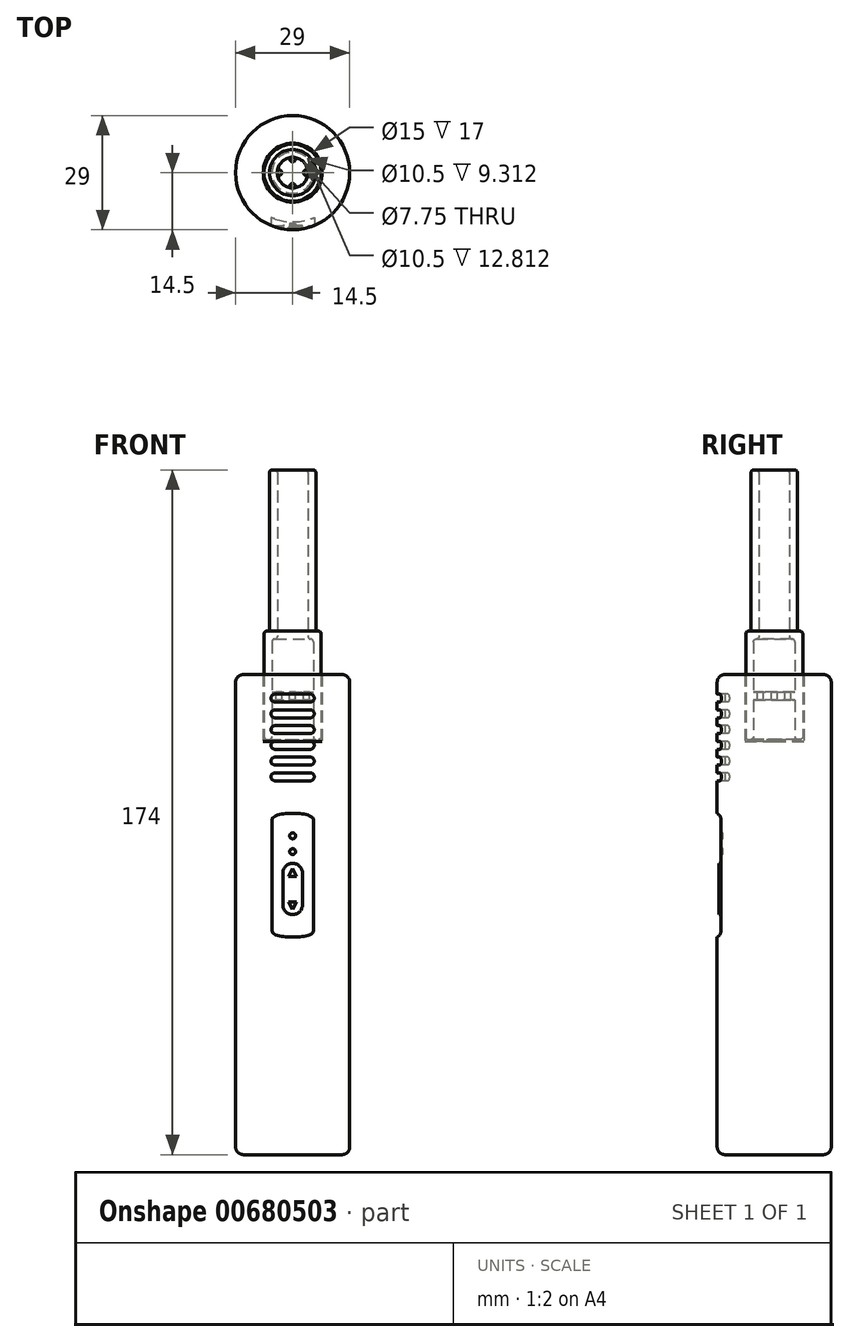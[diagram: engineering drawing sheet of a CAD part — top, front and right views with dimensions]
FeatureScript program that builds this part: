
annotation { "Feature Type Name" : "Feature", "Feature Type Description" : "" }
export const myFeature = defineFeature(function(context is Context, id is Id, definition is map)
    precondition{}
    {
        {
            var Q0;
            Q0=qCreatedBy(makeId("Top.planeOp"),FACE);
            var sketch = newSketch(context, id + "F0", { "sketchPlane" : qUnion([Q0])});
            skCircle(sketch, "E0", {"center": v(0, 0) * mm, "radius": 14.5 * mm});
            skCircle(sketch, "E1", {"center": v(0, 0) * mm, "radius": 7.5 * mm});
            skSolve(sketch);
        }
        {
            var Q0;
            Q0=qCreatedBy(makeId("Front.planeOp"),FACE);
            var sketch = newSketch(context, id + "F1", { "sketchPlane" : qUnion([Q0])});
            skLineSegment(sketch, "E2", {"start": v(0, -17.29) * mm, "end": v(0, 153.89) * mm, "construction": true});
            skSolve(sketch);
        }
        {
            var Q0;
            Q0=makeQuery(id+"F0.imprint","IMPRINT",FACE,{"disambiguationData":[TD([[makeQuery(id+"F0.imprint","IMPRINT",EDGE,{"derivedFrom":sQuery(id+"F0.wireOp",EDGE,"E0")}),1.0]])]});
            extrude(context, id + "F2", {"entities" : qUnion([Q0]), "depth" : 122 * mm, "offsetDistance" : 25 * mm});
        }
        {
            var Q0;
            Q0=makeQuery(id+"F0.imprint","IMPRINT",FACE,{"disambiguationData":[TD([[makeQuery(id+"F0.imprint","IMPRINT",EDGE,{"derivedFrom":sQuery(id+"F0.wireOp",EDGE,"E1")}),1.0]])]});
            extrude(context, id + "F3", {"entities" : qUnion([Q0]), "operationType" : NewBodyOperationType.ADD, "depth" : 105 * mm, "offsetDistance" : 25 * mm});
        }
        {
            var Q0;
            Q0=qCreatedBy(makeId("Front.planeOp"),FACE);
            cPlane(context, id + "F4", {"entities" : qUnion([Q0]), "cplaneType" : CPlaneType.OFFSET, "offset" : 15 * mm, "width" : 150 * mm, "height" : 150 * mm});
        }
        {
            var Q0;
            Q0=qCreatedBy(id+"F4.planeOp",FACE);
            var sketch = newSketch(context, id + "F5", { "sketchPlane" : qUnion([Q0])});
            skLineSegment(sketch, "E3.bottom", {"start": v(-4.5, 117) * mm, "end": v(4.5, 117) * mm});
            skLineSegment(sketch, "E3.top", {"start": v(-4.5, 115) * mm, "end": v(4.5, 115) * mm});
            skLineSegment(sketch, "E3.left", {"start": v(-4.5, 117) * mm, "end": v(-4.5, 115) * mm});
            skLineSegment(sketch, "E3.right", {"start": v(4.5, 117) * mm, "end": v(4.5, 115) * mm});
            skPoint(sketch, "E4", {"position": v(0, 115) * mm});
            skCircle(sketch, "E5", {"center": v(4.5, 116) * mm, "radius": 1 * mm});
            skCircle(sketch, "E6", {"center": v(-4.5, 116) * mm, "radius": 1 * mm});
            skLineSegment(sketch, "E7.bottom", {"start": v(-4.5, 113) * mm, "end": v(4.5, 113) * mm});
            skLineSegment(sketch, "E7.top", {"start": v(-4.5, 111) * mm, "end": v(4.5, 111) * mm});
            skLineSegment(sketch, "E7.left", {"start": v(-4.5, 113) * mm, "end": v(-4.5, 111) * mm});
            skLineSegment(sketch, "E7.right", {"start": v(4.5, 113) * mm, "end": v(4.5, 111) * mm});
            skPoint(sketch, "E8", {"position": v(0, 111) * mm});
            skCircle(sketch, "E9", {"center": v(4.5, 112) * mm, "radius": 1 * mm});
            skCircle(sketch, "E10", {"center": v(-4.5, 112) * mm, "radius": 1 * mm});
            skLineSegment(sketch, "E11.bottom", {"start": v(-4.5, 109) * mm, "end": v(4.5, 109) * mm});
            skLineSegment(sketch, "E11.top", {"start": v(-4.5, 107) * mm, "end": v(4.5, 107) * mm});
            skLineSegment(sketch, "E11.left", {"start": v(-4.5, 109) * mm, "end": v(-4.5, 107) * mm});
            skLineSegment(sketch, "E11.right", {"start": v(4.5, 109) * mm, "end": v(4.5, 107) * mm});
            skPoint(sketch, "E12", {"position": v(0, 107) * mm});
            skCircle(sketch, "E13", {"center": v(4.5, 108) * mm, "radius": 1 * mm});
            skCircle(sketch, "E14", {"center": v(-4.5, 108) * mm, "radius": 1 * mm});
            skLineSegment(sketch, "E15.bottom", {"start": v(-4.5, 105) * mm, "end": v(4.5, 105) * mm});
            skLineSegment(sketch, "E15.top", {"start": v(-4.5, 103) * mm, "end": v(4.5, 103) * mm});
            skLineSegment(sketch, "E15.left", {"start": v(-4.5, 105) * mm, "end": v(-4.5, 103) * mm});
            skLineSegment(sketch, "E15.right", {"start": v(4.5, 105) * mm, "end": v(4.5, 103) * mm});
            skPoint(sketch, "E16", {"position": v(0, 103) * mm});
            skCircle(sketch, "E17", {"center": v(4.5, 104) * mm, "radius": 1 * mm});
            skCircle(sketch, "E18", {"center": v(-4.5, 104) * mm, "radius": 1 * mm});
            skLineSegment(sketch, "E19.bottom", {"start": v(-4.5, 101) * mm, "end": v(4.5, 101) * mm});
            skLineSegment(sketch, "E19.top", {"start": v(-4.5, 99) * mm, "end": v(4.5, 99) * mm});
            skLineSegment(sketch, "E19.left", {"start": v(-4.5, 101) * mm, "end": v(-4.5, 99) * mm});
            skLineSegment(sketch, "E19.right", {"start": v(4.5, 101) * mm, "end": v(4.5, 99) * mm});
            skPoint(sketch, "E20", {"position": v(0, 99) * mm});
            skCircle(sketch, "E21", {"center": v(4.5, 100) * mm, "radius": 1 * mm});
            skCircle(sketch, "E22", {"center": v(-4.5, 100) * mm, "radius": 1 * mm});
            skLineSegment(sketch, "E23.bottom", {"start": v(-4.5, 97) * mm, "end": v(4.5, 97) * mm});
            skLineSegment(sketch, "E23.top", {"start": v(-4.5, 95) * mm, "end": v(4.5, 95) * mm});
            skLineSegment(sketch, "E23.left", {"start": v(-4.5, 97) * mm, "end": v(-4.5, 95) * mm});
            skLineSegment(sketch, "E23.right", {"start": v(4.5, 97) * mm, "end": v(4.5, 95) * mm});
            skPoint(sketch, "E24", {"position": v(0, 95) * mm});
            skCircle(sketch, "E25", {"center": v(4.5, 96) * mm, "radius": 1 * mm});
            skCircle(sketch, "E26", {"center": v(-4.5, 96) * mm, "radius": 1 * mm});
            skSolve(sketch);
        }
        {
            var Q0;
            Q0=qSketchRegion(id+"F5",true);
            var Q1;
            Q1=makeQuery(id+"F2.opExtrude","SWEPT_FACE",FACE,{"disambiguationData":[OSD([sQuery(id+"F0.wireOp",EDGE,"E0")])]});
            extrude(context, id + "F6", {"entities" : qUnion([Q0]), "operationType" : NewBodyOperationType.REMOVE, "endBound" : BoundingType.UP_TO_SURFACE, "oppositeDirection" : true, "depth" : 25 * mm, "endBoundEntityFace" : qUnion([Q1]), "hasOffset" : true, "offsetDistance" : -2 * mm});
        }
        {
            var Q0;
            Q0=makeQuery(id+"F2.opExtrude","CAP_EDGE",EDGE,{"disambiguationData":[OSD([sQuery(id+"F0.wireOp",EDGE,"E0")])],"isStart":false});
            var Q1;
            Q1=makeQuery(id+"F2.opExtrude","CAP_EDGE",EDGE,{"disambiguationData":[OSD([sQuery(id+"F0.wireOp",EDGE,"E0")])],"isStart":true});
            fillet(context, id + "F7", {"entities" : qUnion([Q0, Q1]), "radius" : 2 * mm, "tangentPropagation" : true, "allowEdgeOverflow" : false});
        }
        {
            var Q0;
            Q0=qCreatedBy(makeId("Right.planeOp"),FACE);
            var sketch = newSketch(context, id + "F8", { "sketchPlane" : qUnion([Q0])});
            skLineSegment(sketch, "E27", {"start": v(-15.5, 87) * mm, "end": v(-14.5, 87) * mm});
            skLineSegment(sketch, "E28", {"start": v(-13.5, 85) * mm, "end": v(-13.5, 57) * mm});
            skLineSegment(sketch, "E29", {"start": v(-14.5, 55) * mm, "end": v(-15.5, 55) * mm});
            skLineSegment(sketch, "E30", {"start": v(-14.5, 55) * mm, "end": v(-14.5, 87) * mm});
            skPoint(sketch, "E31.visualSharp", {"position": v(-13.5, 87) * mm});
            skArc(sketch, "E31.filletArc", {"start": v(-13.5, 85) * mm, "mid": v(-14.09, 86.41) * mm, "end": v(-15.5, 87) * mm});
            skPoint(sketch, "E32.visualSharp", {"position": v(-13.5, 55) * mm});
            skArc(sketch, "E32.filletArc", {"start": v(-15.5, 55) * mm, "mid": v(-14.09, 55.59) * mm, "end": v(-13.5, 57) * mm});
            skSolve(sketch);
        }
        {
            var Q0;
            Q0=qSketchRegion(id+"F8",true);
            extrude(context, id + "F9", {"entities" : qUnion([Q0]), "operationType" : NewBodyOperationType.REMOVE, "oppositeDirection" : true, "depth" : 25 * mm, "offsetDistance" : 25 * mm, "symmetric" : true});
        }
        {
            var Q0;
            Q0=makeQuery(id+"F9.boolean.opBoolean","COPY",FACE,{"derivedFrom":makeQuery(id+"F9.opExtrude","SWEPT_FACE",FACE,{"disambiguationData":[OSD([sQuery(id+"F8.wireOp",EDGE,"E28")])]})});
            var sketch = newSketch(context, id + "F10", { "sketchPlane" : qUnion([Q0])});
            skLineSegment(sketch, "E33.bottom", {"start": v(0, 74) * mm, "end": v(0, 74) * mm});
            skLineSegment(sketch, "E33.top", {"start": v(0, 61) * mm, "end": v(0, 61) * mm});
            skLineSegment(sketch, "E33.left", {"start": v(-2.5, 71.5) * mm, "end": v(-2.5, 63.5) * mm});
            skLineSegment(sketch, "E33.right", {"start": v(2.5, 71.5) * mm, "end": v(2.5, 63.5) * mm});
            skPoint(sketch, "E34", {"position": v(0, 74) * mm});
            skPoint(sketch, "E35.visualSharp", {"position": v(-2.5, 74) * mm});
            skArc(sketch, "E35.filletArc", {"start": v(0, 74) * mm, "mid": v(-1.77, 73.27) * mm, "end": v(-2.5, 71.5) * mm});
            skPoint(sketch, "E36.visualSharp", {"position": v(2.5, 74) * mm});
            skArc(sketch, "E36.filletArc", {"start": v(2.5, 71.5) * mm, "mid": v(1.77, 73.27) * mm, "end": v(0, 74) * mm});
            skPoint(sketch, "E37.visualSharp", {"position": v(2.5, 61) * mm});
            skArc(sketch, "E37.filletArc", {"start": v(0, 61) * mm, "mid": v(1.77, 61.73) * mm, "end": v(2.5, 63.5) * mm});
            skPoint(sketch, "E38.visualSharp", {"position": v(-2.5, 61) * mm});
            skArc(sketch, "E38.filletArc", {"start": v(-2.5, 63.5) * mm, "mid": v(-1.77, 61.73) * mm, "end": v(0, 61) * mm});
            skLineSegment(sketch, "E39", {"start": v(0, 72.75) * mm, "end": v(-1, 70.75) * mm});
            skLineSegment(sketch, "E40", {"start": v(-1, 70.75) * mm, "end": v(1, 70.75) * mm});
            skLineSegment(sketch, "E41", {"start": v(1, 70.75) * mm, "end": v(0, 72.75) * mm});
            skLineSegment(sketch, "E42", {"start": v(0, 62.25) * mm, "end": v(1, 64.25) * mm});
            skLineSegment(sketch, "E43", {"start": v(1, 64.25) * mm, "end": v(-1, 64.25) * mm});
            skLineSegment(sketch, "E44", {"start": v(-1, 64.25) * mm, "end": v(0, 62.25) * mm});
            skCircle(sketch, "E45", {"center": v(0, 81) * mm, "radius": 0.75 * mm});
            skCircle(sketch, "E46", {"center": v(0, 77) * mm, "radius": 0.75 * mm});
            skSolve(sketch);
        }
        {
            var Q0;
            Q0=makeQuery(id+"F10.imprint","IMPRINT",FACE,{"disambiguationData":[TD([[makeQuery(id+"F10.imprint","IMPRINT",EDGE,{"derivedFrom":sQuery(id+"F10.wireOp",EDGE,"E33.left")}),1.0]])]});
            extrude(context, id + "F11", {"entities" : qUnion([Q0]), "operationType" : NewBodyOperationType.ADD, "depth" : .6 * mm, "offsetDistance" : 25 * mm});
        }
        {
            var Q0;
            Q0=makeQuery(id+"F10.imprint","IMPRINT",FACE,{"disambiguationData":[TD([[makeQuery(id+"F10.imprint","IMPRINT",EDGE,{"derivedFrom":sQuery(id+"F10.wireOp",EDGE,"E39")}),1.0]])]});
            var Q1;
            Q1=makeQuery(id+"F10.imprint","IMPRINT",FACE,{"disambiguationData":[TD([[makeQuery(id+"F10.imprint","IMPRINT",EDGE,{"derivedFrom":sQuery(id+"F10.wireOp",EDGE,"E42")}),1.0]])]});
            extrude(context, id + "F12", {"entities" : qUnion([Q0, Q1]), "operationType" : NewBodyOperationType.ADD, "depth" : 0.4 * mm, "offsetDistance" : 25 * mm});
        }
        {
            var Q0;
            Q0=makeQuery(id+"F10.imprint","IMPRINT",FACE,{"disambiguationData":[TD([[makeQuery(id+"F10.imprint","IMPRINT",EDGE,{"derivedFrom":sQuery(id+"F10.wireOp",EDGE,"E45")}),1.0]])]});
            var Q1;
            Q1=makeQuery(id+"F10.imprint","IMPRINT",FACE,{"disambiguationData":[TD([[makeQuery(id+"F10.imprint","IMPRINT",EDGE,{"derivedFrom":sQuery(id+"F10.wireOp",EDGE,"E46")}),1.0]])]});
            extrude(context, id + "F13", {"entities" : qUnion([Q0, Q1]), "operationType" : NewBodyOperationType.REMOVE, "oppositeDirection" : true, "depth" : .5 * mm, "offsetDistance" : 25 * mm});
        }
        {
            var Q0;
            Q0=qCreatedBy(makeId("Front.planeOp"),FACE);
            var sketch = newSketch(context, id + "F14", { "sketchPlane" : qUnion([Q0])});
            skLineSegment(sketch, "E47.bottom", {"start": v(5.88, 133) * mm, "end": v(7.25, 133) * mm});
            skLineSegment(sketch, "E47.top", {"start": v(5.25, 105.5) * mm, "end": v(7.25, 105.5) * mm});
            skLineSegment(sketch, "E47.left", {"start": v(5.25, 131) * mm, "end": v(5.25, 105.5) * mm});
            skLineSegment(sketch, "E47.right", {"start": v(7.25, 133) * mm, "end": v(7.25, 105.5) * mm});
            skLineSegment(sketch, "E48.bottom", {"start": v(5.25, 117.5) * mm, "end": v(0, 117.5) * mm});
            skLineSegment(sketch, "E48.top", {"start": v(5.25, 115.5) * mm, "end": v(0, 115.5) * mm});
            skLineSegment(sketch, "E48.left", {"start": v(5.25, 117.5) * mm, "end": v(5.25, 115.5) * mm});
            skLineSegment(sketch, "E48.right", {"start": v(0, 117.5) * mm, "end": v(0, 115.5) * mm});
            skLineSegment(sketch, "E49.bottom", {"start": v(3.87, 174) * mm, "end": v(5.87, 174) * mm});
            skLineSegment(sketch, "E49.top", {"start": v(3.88, 131) * mm, "end": v(5.25, 131) * mm});
            skLineSegment(sketch, "E49.left", {"start": v(3.87, 174) * mm, "end": v(3.88, 131) * mm});
            skLineSegment(sketch, "E49.right", {"start": v(5.87, 174) * mm, "end": v(5.88, 133) * mm});
            skPoint(sketch, "E50", {"position": v(5.88, 133) * mm});
            skPoint(sketch, "E51", {"position": v(5.25, 131) * mm});
            skSolve(sketch);
        }
        {
            var Q0;
            Q0=qSketchRegion(id+"F14",true);
            var Q1;
            Q1=sQuery(id+"F1.wireOp",EDGE,"E2");
            revolve(context, id + "F15", {"surfaceOperationType" : NewSurfaceOperationType.NEW, "entities" : qUnion([Q0]), "axis" : qUnion([Q1]), "revolveType" : RevolveType.FULL});
        }
        {
            var Q0;
            Q0=makeQuery(id+"F15.opRevolve","SWEPT_EDGE",EDGE,{"disambiguationData":[OSD([sQuery(id+"F14.wireOp",EDGE,"E47.bottom"),sQuery(id+"F14.wireOp",EDGE,"E47.right")])]});
            var Q1;
            Q1=makeQuery(id+"F15.opRevolve","SWEPT_EDGE",EDGE,{"disambiguationData":[OSD([sQuery(id+"F14.wireOp",EDGE,"E47.bottom"),sQuery(id+"F14.wireOp",EDGE,"E49.right")])]});
            var Q2;
            Q2=makeQuery(id+"F15.opRevolve","SWEPT_EDGE",EDGE,{"disambiguationData":[OSD([sQuery(id+"F14.wireOp",EDGE,"E47.top"),sQuery(id+"F14.wireOp",EDGE,"E47.left")])]});
            var Q3;
            Q3=makeQuery(id+"F15.opRevolve","SWEPT_EDGE",EDGE,{"disambiguationData":[OSD([sQuery(id+"F14.wireOp",EDGE,"E47.top"),sQuery(id+"F14.wireOp",EDGE,"E47.right")])]});
            var Q4;
            Q4=makeQuery(id+"F15.opRevolve","SWEPT_EDGE",EDGE,{"disambiguationData":[OSD([sQuery(id+"F14.wireOp",EDGE,"E47.left"),sQuery(id+"F14.wireOp",EDGE,"E49.top")])]});
            var Q5;
            Q5=makeQuery(id+"F15.opRevolve","SWEPT_EDGE",EDGE,{"disambiguationData":[OSD([sQuery(id+"F14.wireOp",EDGE,"E49.top"),sQuery(id+"F14.wireOp",EDGE,"E49.left")])]});
            var Q6;
            Q6=makeQuery(id+"F15.opRevolve","SWEPT_EDGE",EDGE,{"disambiguationData":[OSD([sQuery(id+"F14.wireOp",EDGE,"E49.bottom"),sQuery(id+"F14.wireOp",EDGE,"E49.right")])]});
            var Q7;
            Q7=makeQuery(id+"F15.opRevolve","SWEPT_EDGE",EDGE,{"disambiguationData":[OSD([sQuery(id+"F14.wireOp",EDGE,"E49.bottom"),sQuery(id+"F14.wireOp",EDGE,"E49.left")])]});
            fillet(context, id + "F16", {"entities" : qUnion([Q0, Q1, Q2, Q3, Q4, Q5, Q6, Q7]), "radius" : .6875 * mm, "tangentPropagation" : true, "allowEdgeOverflow" : false});
        }
        {
            var Q0;
            Q0=makeQuery(id+"F15.opRevolve","SWEPT_FACE",FACE,{"disambiguationData":[OSD([sQuery(id+"F14.wireOp",EDGE,"E48.bottom")])]});
            var sketch = newSketch(context, id + "F17", { "sketchPlane" : qUnion([Q0])});
            skCircle(sketch, "E52", {"center": v(0, 3.5) * mm, "radius": 0.75 * mm});
            skCircle(sketch, "E53.1.0", {"center": v(-3.5, 0) * mm, "radius": 0.75 * mm});
            skCircle(sketch, "E53.2.0", {"center": v(0, -3.5) * mm, "radius": 0.75 * mm});
            skCircle(sketch, "E53.3.0", {"center": v(3.5, 0) * mm, "radius": 0.75 * mm});
            skPoint(sketch, "E53.center", {"position": v(0, 0) * mm});
            skSolve(sketch);
        }
        {
            var Q0;
            Q0=qSketchRegion(id+"F17",true);
            extrude(context, id + "F18", {"entities" : qUnion([Q0]), "operationType" : NewBodyOperationType.REMOVE, "endBound" : BoundingType.UP_TO_NEXT, "oppositeDirection" : true, "depth" : 25 * mm, "offsetDistance" : 25 * mm});
        }
    });
